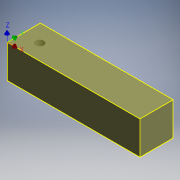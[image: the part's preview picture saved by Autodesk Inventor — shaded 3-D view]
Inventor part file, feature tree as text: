
AUTODESK INVENTOR PART (.ipt)
format: ipt  version: 2018 (Build 220112000, 112)  size: 331,776 bytes
history: native  units: mm (DEFAULTED — no unit token found)
features: extrude x4, other x4, sketch x2, fillet x1, loft x1
ambient origin geometry x8: Origin, YZ Plane, XZ Plane, XY Plane, X Axis, Y Axis, Z Axis, Center Point
bodies: Solid1 (feature_tree)
feature tree (12):
  extrude  "Extrusion1"  Depth=25.4mm
  sketch  "Sketch2"  dims[d2=25.4mm d3=0.0mm d4=3.6576mm d5=6.2738mm d6=5.8166mm d7=19.812mm d8=0.0mm d9=9.398mm d10=0.0mm d11=4.1148mm d12=0.0mm d13=1.8288mm d14=0.0mm d15=90.0deg d16=0.0mm d17=90.0deg d18=0.0mm d19=90.0deg d20=0.0mm d21=90.0deg]
  extrude  "Extrusion2"  Depth=3.6576mm
  extrude  "Extrusion3"  Depth=6.2738mm
  extrude  "Extrusion4"  Depth=5.8166mm
  fillet  "Fillet1"  Radius=19.812mm
  loft  "Loft1"
  sketch  "Sketch1"  dims[d0=101.6mm d1=25.4mm]
  other  "Edges1"
  other  "Edges2"
  other  "Edges3"
  other  "Edges4"
